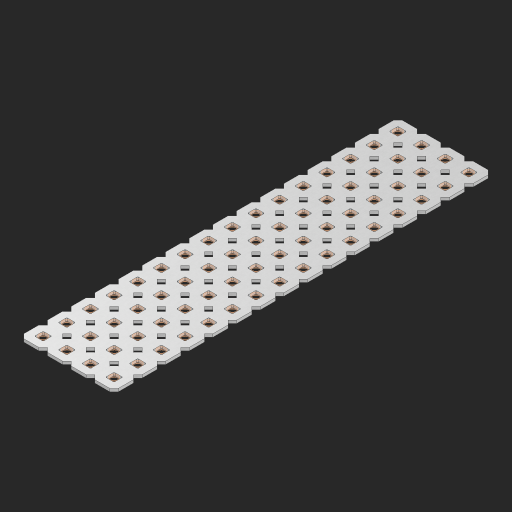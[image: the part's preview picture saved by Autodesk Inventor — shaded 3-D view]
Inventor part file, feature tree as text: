
AUTODESK INVENTOR PART (.ipt)
format: ipt  version: 2023 (Build 270158000, 158)  size: 1,026,048 bytes
history: native  units: in
note: dims shown in document units (in); Inventor stores cm internally (conversion verified against a paired STEP export)
features: other x65, extrude x63, sketch x2, pattern_linear x1
ambient origin geometry x8: Origin, YZ Plane, XZ Plane, XY Plane, X Axis, Y Axis, Z Axis, Center Point
bodies: Solid1 (feature_tree), Body (feature_tree)
feature tree (131):
  pattern_linear  "Rectangular Pattern1"  Spacing1=0.09in  [1 undecoded]
  sketch  "Sketch1"  dims[d1=0.5in]
  sketch  "Sketch2"  dims[d2=0.182in d3=0.09in d4=0.09in d5=0.09in d6=0.09in d7=0.09in d8=0.09in d9=0.09in d10=0.09in d11=0.02in d13=0.0in d14=0.172in d15=0.0625in d16=0.0in d19=0.5in d22=0.5in]
  other  "Srf1"
  other  "Srf126"
  other  "Srf127"
  other  "Srf128"
  other  "Srf129"
  other  "Srf130"
  other  "Srf131"
  other  "Srf250"
  other  "Srf251"
  other  "Srf252"
  other  "Srf253"
  other  "Srf254"
  other  "Srf255"
  other  "Srf256"
  other  "Srf257"
  other  "Srf258"
  other  "Srf268"
  other  "Srf269"
  other  "Srf270"
  other  "Srf271"
  other  "Srf272"
  other  "Srf273"
  other  "Srf274"
  other  "Srf275"
  other  "Srf276"
  other  "Srf277"
  other  "Srf278"
  other  "Srf279"
  other  "Srf280"
  other  "Srf281"
  other  "Srf282"
  other  "Srf283"
  other  "Srf293"
  other  "Srf294"
  other  "Srf295"
  other  "Srf296"
  other  "Srf297"
  other  "Srf298"
  other  "Srf299"
  other  "Srf300"
  other  "Srf301"
  other  "Srf302"
  other  "Srf303"
  other  "Srf304"
  other  "Srf305"
  other  "Srf306"
  other  "Srf307"
  other  "Srf308"
  other  "Srf318"
  other  "Srf319"
  other  "Srf320"
  other  "Srf321"
  other  "Srf322"
  other  "Srf323"
  other  "Srf324"
  other  "Srf325"
  other  "Srf326"
  other  "Srf327"
  other  "Srf328"
  other  "Srf329"
  other  "Srf330"
  other  "Srf331"
  other  "Srf332"
  other  "Srf333"
  other  "Circle"
  extrude  "ExtrusionSrf126"  Depth=0.09in
  extrude  "ExtrusionSrf127"  Depth=0.09in
  extrude  "ExtrusionSrf128"  Depth=0.09in
  extrude  "ExtrusionSrf129"  Depth=0.09in
  extrude  "ExtrusionSrf130"  Depth=0.09in
  extrude  "ExtrusionSrf131"  Depth=0.09in
  extrude  "ExtrusionSrf250"  Depth=0.09in
  extrude  "ExtrusionSrf251"  Depth=0.02in
  extrude  "ExtrusionSrf252"  TaperAngle=0.0deg  [1 undecoded]
  extrude  "ExtrusionSrf253"  Depth=0.5in
  extrude  "ExtrusionSrf254"  Depth=0.0625in TaperAngle=0.0deg
  extrude  "ExtrusionSrf255"  Depth=0.5in
  extrude  "ExtrusionSrf256"  Depth=0.5in
  extrude  "ExtrusionSrf257"  [1 undecoded]
  extrude  "ExtrusionSrf258"  [1 undecoded]
  extrude  "ExtrusionSrf268"  [1 undecoded]
  extrude  "ExtrusionSrf269"  [1 undecoded]
  extrude  "ExtrusionSrf270"  [1 undecoded]
  extrude  "ExtrusionSrf271"  [1 undecoded]
  extrude  "ExtrusionSrf272"  [1 undecoded]
  extrude  "ExtrusionSrf273"  [1 undecoded]
  extrude  "ExtrusionSrf274"  [1 undecoded]
  extrude  "ExtrusionSrf275"  [1 undecoded]
  extrude  "ExtrusionSrf276"  [1 undecoded]
  extrude  "ExtrusionSrf277"  [1 undecoded]
  extrude  "ExtrusionSrf278"  [1 undecoded]
  extrude  "ExtrusionSrf279"  [1 undecoded]
  extrude  "ExtrusionSrf280"  [1 undecoded]
  extrude  "ExtrusionSrf281"  [1 undecoded]
  extrude  "ExtrusionSrf282"  [1 undecoded]
  extrude  "ExtrusionSrf283"  [1 undecoded]
  extrude  "ExtrusionSrf293"  [1 undecoded]
  extrude  "ExtrusionSrf294"  [1 undecoded]
  extrude  "ExtrusionSrf295"  [1 undecoded]
  extrude  "ExtrusionSrf296"  [1 undecoded]
  extrude  "ExtrusionSrf297"  [1 undecoded]
  extrude  "ExtrusionSrf298"  [1 undecoded]
  extrude  "ExtrusionSrf299"  [1 undecoded]
  extrude  "ExtrusionSrf300"  [1 undecoded]
  extrude  "ExtrusionSrf301"  [1 undecoded]
  extrude  "ExtrusionSrf302"  [1 undecoded]
  extrude  "ExtrusionSrf303"  [1 undecoded]
  extrude  "ExtrusionSrf304"  [1 undecoded]
  extrude  "ExtrusionSrf305"  [1 undecoded]
  extrude  "ExtrusionSrf306"  [1 undecoded]
  extrude  "ExtrusionSrf307"  [1 undecoded]
  extrude  "ExtrusionSrf308"  [1 undecoded]
  extrude  "ExtrusionSrf318"  [1 undecoded]
  extrude  "ExtrusionSrf319"  [1 undecoded]
  extrude  "ExtrusionSrf320"  [1 undecoded]
  extrude  "ExtrusionSrf321"  [1 undecoded]
  extrude  "ExtrusionSrf322"  [1 undecoded]
  extrude  "ExtrusionSrf323"  [1 undecoded]
  extrude  "ExtrusionSrf324"  [1 undecoded]
  extrude  "ExtrusionSrf325"  [1 undecoded]
  extrude  "ExtrusionSrf326"  [1 undecoded]
  extrude  "ExtrusionSrf327"  [1 undecoded]
  extrude  "ExtrusionSrf328"  [1 undecoded]
  extrude  "ExtrusionSrf329"  [1 undecoded]
  extrude  "ExtrusionSrf330"  [1 undecoded]
  extrude  "ExtrusionSrf331"  [1 undecoded]
  extrude  "ExtrusionSrf332"  [1 undecoded]
  extrude  "ExtrusionSrf333"  [1 undecoded]
note: 52 required parameter values undecoded (feature->parameter linkage not recoverable at this tier; creation-order binding heuristic only, values carry confidence <= 0.55)
